# Revit family: MOD 3L-W-ID
name_source: partatom
category: Lighting Fixtures
units: mm (PartAtom-declared; Revit-internal decimal feet)

## family parameters
Cut with Voids When Loaded = No
Host = Face
Light Source = No
OmniClass Number = 23.80.70.11.14.17
OmniClass Title = Direct/Indirect
Part Type = Normal
Room Calculation Point = No
Round Connector Dimension = Use Diameter
Shared = No

## types (6) — shared parameters
Apparent Load = 25 VA
Connector Description = Lighting Connector
Default Elevation = 4 '
Description = MOD™ 3 LED Wall Indirect/Direct
Lamp = LED
Load Classification = Lighting
Manufacturer = LITECONTROL
Model = 3L-W-ID
Photometric Web = Web MOD 3L : 3L-W-ID-LPA-4-SOF-X-CX-35K-I100-D100
Reflector Finish = White Glass
URL = https://www.currentlighting.com
Wattage Comments = 10W
Watts = 10 W

## per-type parameters (varying)
| type | Product Material |
| Textured Matte White | Paint -  Textured Matte White |
| Matte White | Paint -  Matte White |
| Light Silver | Paint - Light Silver |
| Machined Aluminium | Paint -  Machined Aluminum |
| Carbon Black | Paint -  Carbon Black |
| Textured Camera Black | Paint -  Textured Camera Black |

## geometry (parser evidence)
native form markers: Blend x7, Sweep x8
no freeform markers — native parametric forms only
